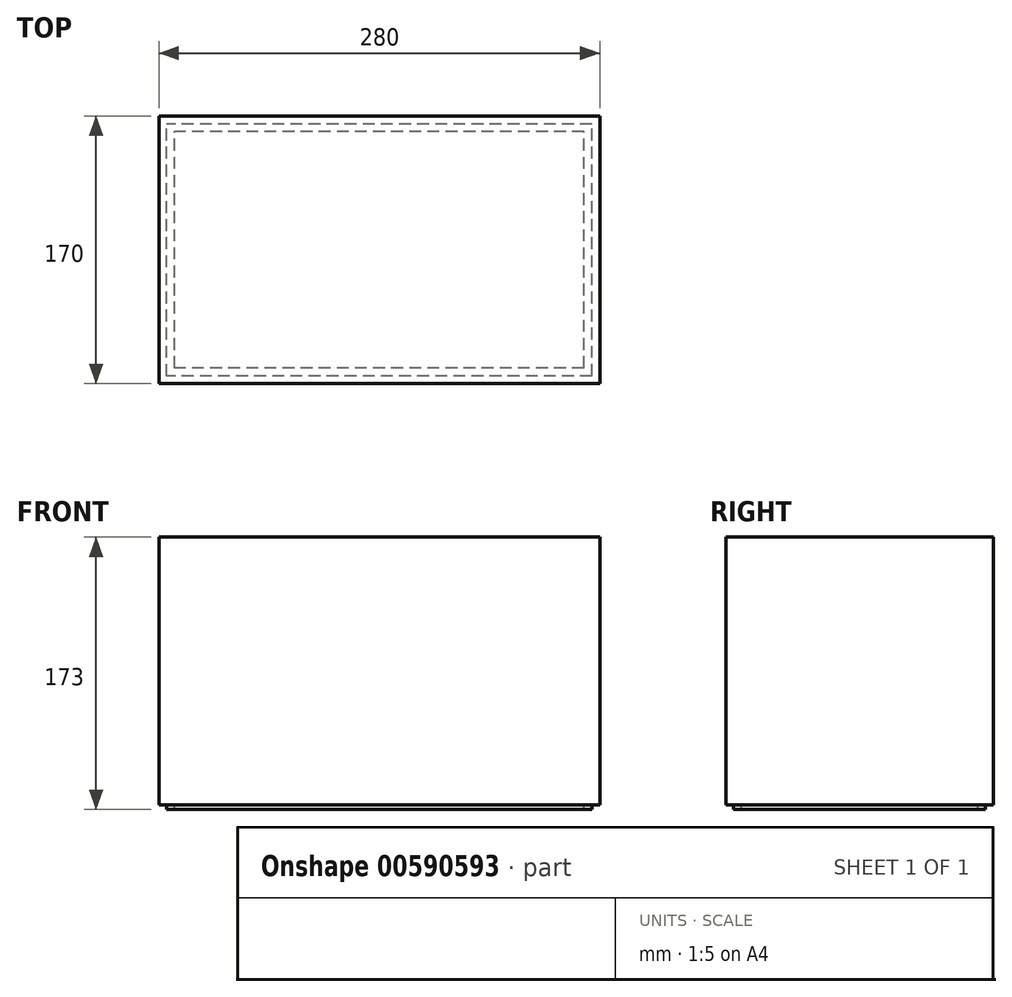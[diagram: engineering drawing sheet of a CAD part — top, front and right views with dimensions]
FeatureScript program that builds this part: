
annotation { "Feature Type Name" : "Feature", "Feature Type Description" : "" }
export const myFeature = defineFeature(function(context is Context, id is Id, definition is map)
    precondition{}
    {
        {
            var Q0;
            Q0=qCreatedBy(makeId("Top.planeOp"),FACE);
            var sketch = newSketch(context, id + "F0", { "sketchPlane" : qUnion([Q0])});
            skLineSegment(sketch, "E0.bottom", {"start": v(140, 85) * mm, "end": v(-140, 85) * mm});
            skLineSegment(sketch, "E0.top", {"start": v(140, -85) * mm, "end": v(-140, -85) * mm});
            skLineSegment(sketch, "E0.left", {"start": v(140, 85) * mm, "end": v(140, -85) * mm});
            skLineSegment(sketch, "E0.right", {"start": v(-140, 85) * mm, "end": v(-140, -85) * mm});
            skPoint(sketch, "E0.middle", {"position": v(0, 0) * mm});
            skSolve(sketch);
        }
        {
            var Q0;
            Q0 = qSketchRegion(id + "F0", true);
            extrude(context, id + "F1", {"entities" : qUnion([Q0]), "depth" : 170 * mm, "offsetDistance" : 25 * mm});
        }
        {
            var Q0;
            Q0=makeQuery(id+"F1.opExtrude","CAP_FACE",FACE,{"disambiguationData":[OSD([sQuery(id+"F0.wireOp",EDGE,"E0.bottom"),sQuery(id+"F0.wireOp",EDGE,"E0.top"),sQuery(id+"F0.wireOp",EDGE,"E0.left"),sQuery(id+"F0.wireOp",EDGE,"E0.right")])],"isStart":true});
            var sketch = newSketch(context, id + "F2", { "sketchPlane" : qUnion([Q0])});
            skLineSegment(sketch, "E1.bottom", {"start": v(135, 80) * mm, "end": v(-135, 80) * mm});
            skLineSegment(sketch, "E1.top", {"start": v(135, -80) * mm, "end": v(-135, -80) * mm});
            skLineSegment(sketch, "E1.left", {"start": v(135, 80) * mm, "end": v(135, -80) * mm});
            skLineSegment(sketch, "E1.right", {"start": v(-135, 80) * mm, "end": v(-135, -80) * mm});
            skPoint(sketch, "E1.middle", {"position": v(0, 0) * mm});
            skLineSegment(sketch, "E2.bottom", {"start": v(130, 75) * mm, "end": v(-130, 75) * mm});
            skLineSegment(sketch, "E2.top", {"start": v(130, -75) * mm, "end": v(-130, -75) * mm});
            skLineSegment(sketch, "E2.left", {"start": v(130, 75) * mm, "end": v(130, -75) * mm});
            skLineSegment(sketch, "E2.right", {"start": v(-130, 75) * mm, "end": v(-130, -75) * mm});
            skSolve(sketch);
        }
        {
            var Q0;
            Q0 = qSketchRegion(id + "F2", true);
            extrude(context, id + "F3", {"entities" : qUnion([Q0]), "operationType" : NewBodyOperationType.ADD, "depth" : 3 * mm, "offsetDistance" : 25 * mm});
        }
    });
